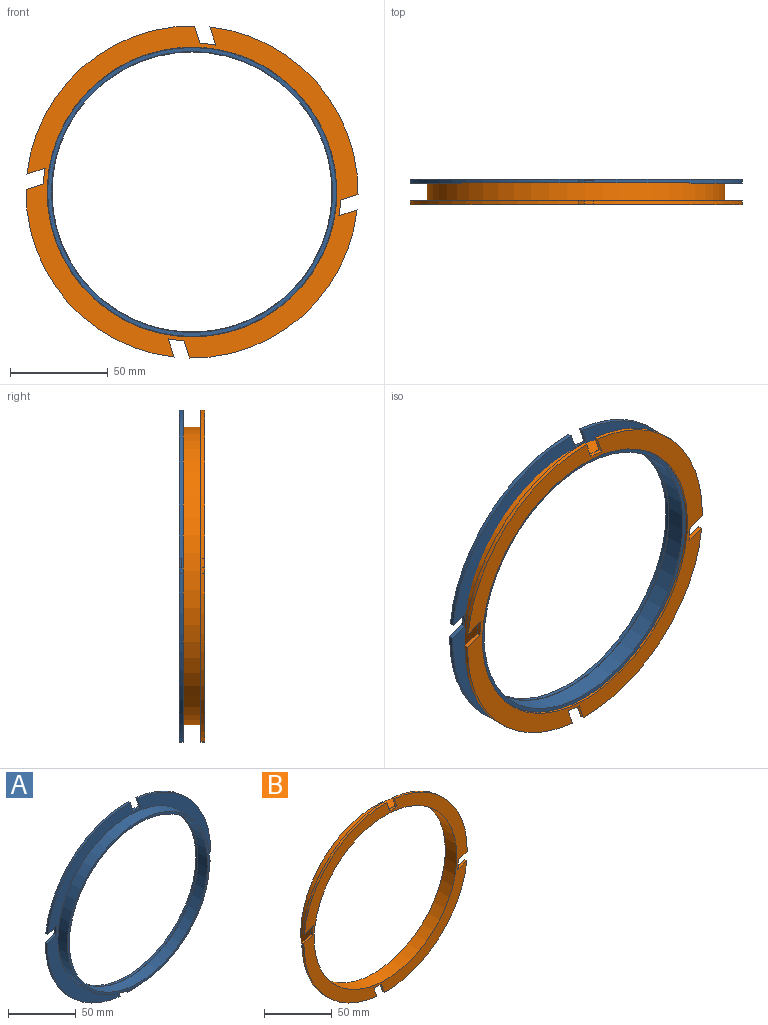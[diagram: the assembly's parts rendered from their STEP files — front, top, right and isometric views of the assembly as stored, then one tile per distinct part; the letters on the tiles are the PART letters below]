
ASSEMBLY  parts=2 mates=1
PART A: 23 faces, bbox 170x12x170 mm
  f0: plane 170x170mm, normal (0,-1,0), area 5237.8mm2, adj f2,f3,f4,f5,f7,f11,f12,f13
  f1: plane 170x170mm, normal (0,1,0), area 6267.3mm2, adj f2,f3,f4,f5,f10,f11,f12,f13
  f2: cylinder r=85mm len=85.74mm, axis (0,-1,0), area 251.2mm2, adj f0,f1,f19,f21
  f3: cylinder r=85mm len=85.74mm, axis (0,-1,0), area 251.2mm2, adj f0,f1,f16,f18
  f4: cylinder r=85mm len=85.74mm, axis (0,-1,0), area 251.2mm2, adj f0,f1,f13,f15
  f5: cylinder r=85mm len=85.74mm, axis (0,-1,0), area 251.2mm2, adj f0,f1,f12,f22
  f6: cylinder r=71.95mm len=143.9mm, axis (0,-1,0), area 4520.8mm2, adj f8,f9
  f7: cylinder r=73.95mm len=147.9mm, axis (0,-1,0), area 4646.4mm2, adj f0,f8
  f8: plane 147.9x147.9mm, normal (0,-1,0), area 916.7mm2, adj f6,f7
  f9: plane 143.9x143.9mm, normal (0,-1,0), area 112.8mm2, adj f6,f10
  f10: cylinder r=71.7mm len=143.4mm, axis (0,1,0), area 901mm2, adj f1,f9
  f11: cylinder r=76.21mm len=8mm, axis (0,-1,0), area 16.1mm2, adj f0,f1,f12,f13
  f12: plane 9.27x3.02mm, normal (0.31,0,-0.95), area 19.5mm2, adj f0,f1,f5,f11
  f13: plane 8.89x2.89mm, normal (-0.31,0,0.95), area 18.7mm2, adj f0,f1,f4,f11
  f14: cylinder r=76.21mm len=8mm, axis (0,-1,0), area 16.1mm2, adj f0,f1,f15,f16
  f15: plane 9.27x3.02mm, normal (0.95,0,0.31), area 19.5mm2, adj f0,f1,f4,f14
  f16: plane 8.89x2.89mm, normal (-0.95,0,-0.31), area 18.7mm2, adj f0,f1,f3,f14
  f17: cylinder r=76.21mm len=8mm, axis (0,-1,0), area 16.1mm2, adj f0,f1,f18,f19
  f18: plane 9.27x3.02mm, normal (-0.31,0,0.95), area 19.5mm2, adj f0,f1,f3,f17
  f19: plane 8.89x2.89mm, normal (0.31,0,-0.95), area 18.7mm2, adj f0,f1,f2,f17
  f20: cylinder r=76.21mm len=8mm, axis (0,-1,0), area 16.1mm2, adj f0,f1,f21,f22
  f21: plane 9.27x3.02mm, normal (-0.95,0,-0.31), area 19.5mm2, adj f0,f1,f2,f20
  f22: plane 8.89x2.89mm, normal (0.95,0,0.31), area 18.7mm2, adj f0,f1,f5,f20
PART B: 21 faces, bbox 170x12x170 mm
  f0: plane 170x170mm, normal (0,-1,0), area 5121.4mm2, adj f2,f3,f4,f5,f8,f9,f10,f11
  f1: plane 170x170mm, normal (0,1,0), area 4176.5mm2, adj f2,f3,f4,f5,f6,f9,f10,f11
  f2: cylinder r=85mm len=85.74mm, axis (0,1,0), area 251.2mm2, adj f0,f1,f17,f19
  f3: cylinder r=85mm len=85.74mm, axis (0,1,0), area 251.2mm2, adj f0,f1,f13,f16
  f4: cylinder r=85mm len=85.74mm, axis (0,1,0), area 251.2mm2, adj f0,f1,f10,f12
  f5: cylinder r=85mm len=85.74mm, axis (0,1,0), area 251.2mm2, adj f0,f1,f9,f20
  f6: cylinder r=76.2mm len=152.4mm, axis (0,-1,0), area 4787.8mm2, adj f1,f7
  f7: plane 152.4x152.4mm, normal (0,1,0), area 945mm2, adj f6,f8
  f8: cylinder r=74.2mm len=148.4mm, axis (0,-1,0), area 5594.5mm2, adj f0,f7
  f9: plane 9.27x3.02mm, normal (0.31,0,-0.95), area 19.5mm2, adj f0,f1,f5,f11
  f10: plane 8.89x2.89mm, normal (-0.31,0,0.95), area 18.7mm2, adj f0,f1,f4,f11
  f11: cylinder r=76.21mm len=8mm, axis (0,-1,0), area 16.1mm2, adj f0,f1,f9,f10
  f12: plane 9.27x3.02mm, normal (0.95,0,0.31), area 19.5mm2, adj f0,f1,f4,f14
  f13: plane 8.89x2.89mm, normal (-0.95,0,-0.31), area 18.7mm2, adj f0,f1,f3,f14
  f14: cylinder r=76.21mm len=8mm, axis (0,-1,0), area 16.1mm2, adj f0,f1,f12,f13
  f15: cylinder r=76.21mm len=8mm, axis (0,-1,0), area 16.1mm2, adj f0,f1,f16,f17
  f16: plane 9.27x3.02mm, normal (-0.31,0,0.95), area 19.5mm2, adj f0,f1,f3,f15
  f17: plane 8.89x2.89mm, normal (0.31,0,-0.95), area 18.7mm2, adj f0,f1,f2,f15
  f18: cylinder r=76.21mm len=8mm, axis (0,-1,0), area 16.1mm2, adj f0,f1,f19,f20
  f19: plane 9.27x3.02mm, normal (-0.95,0,-0.31), area 19.5mm2, adj f0,f1,f2,f18
  f20: plane 8.89x2.89mm, normal (0.95,0,0.31), area 18.7mm2, adj f0,f1,f5,f18
PLACE A t=(9.08,-10.7,13.58)mm
PLACE B t=(9.08,0.3,13.58)mm
MATE fastened B.f8 <-> A.f6  axis (0,-1,0) through (9.08,4.3,13.58)mm
